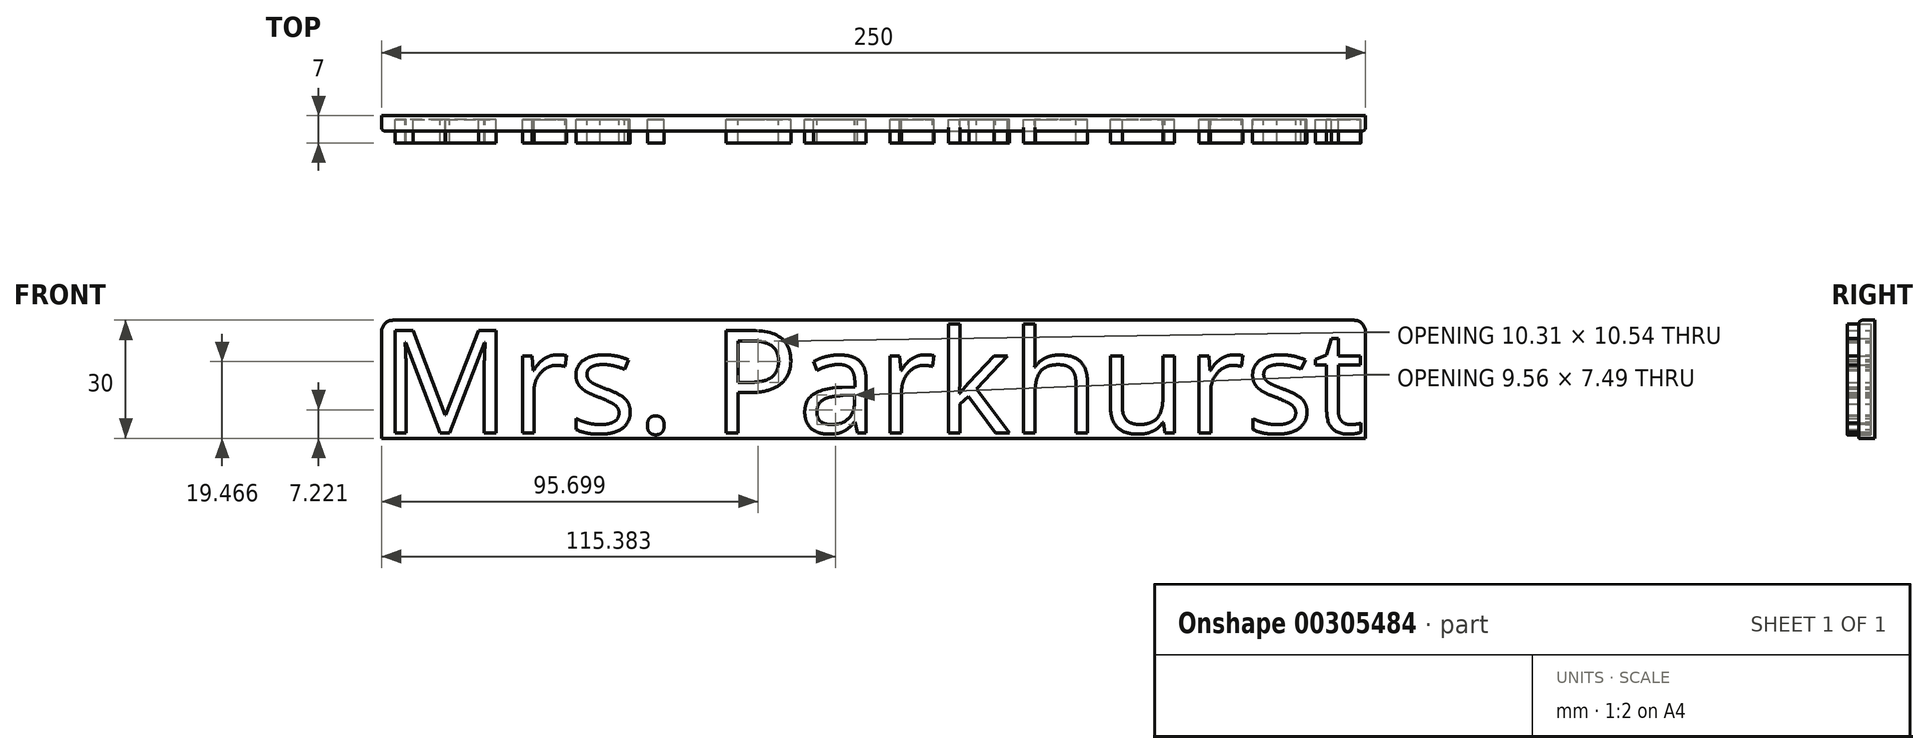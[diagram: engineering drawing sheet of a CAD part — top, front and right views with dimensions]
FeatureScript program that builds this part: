
annotation { "Feature Type Name" : "Feature", "Feature Type Description" : "" }
export const myFeature = defineFeature(function(context is Context, id is Id, definition is map)
    precondition{}
    {
        {
            var Q0;
            Q0=qCreatedBy(makeId("Front.planeOp"),FACE);
            var sketch = newSketch(context, id + "F0", { "sketchPlane" : qUnion([Q0])});
            skText(sketch, "E0", { "text": "Mrs. Parkhurst", "fontName": "OpenSans-Regular.ttf"});
            const initialGuessF0  = {"E0": [-0.12017, 0.0014, 1, 0, 0.02617]};
            skSetInitialGuess(sketch, initialGuessF0);
            skSolve(sketch);
        }
        {
            var Q0;
            Q0=qCreatedBy(makeId("Front.planeOp"),FACE);
            var sketch = newSketch(context, id + "F1", { "sketchPlane" : qUnion([Q0])});
            skLineSegment(sketch, "E1.bottom", {"start": v(-120.02, 30) * mm, "end": v(129.98, 30) * mm});
            skLineSegment(sketch, "E1.top", {"start": v(-120.02, 0) * mm, "end": v(129.98, 0) * mm});
            skLineSegment(sketch, "E1.left", {"start": v(-120.02, 30) * mm, "end": v(-120.02, 0) * mm});
            skLineSegment(sketch, "E1.right", {"start": v(129.98, 30) * mm, "end": v(129.98, 0) * mm});
            skSolve(sketch);
        }
        {
            var Q0;
            Q0 = qSketchRegion(id + "F0", true);
            extrude(context, id + "F2", {"entities" : qUnion([Q0]), "endBound" : BoundingType.SYMMETRIC, "depth" : 6 * mm});
        }
        {
            var Q0;
            Q0 = qSketchRegion(id + "F1", true);
            extrude(context, id + "F3", {"entities" : qUnion([Q0]), "oppositeDirection" : true, "depth" : 4 * mm});
        }
        {
            var Q0;
            Q0=makeQuery(id+"F3.opExtrude","SWEPT_EDGE",EDGE,{"disambiguationData":[OSD([sQuery(id+"F1.wireOp",EDGE,"E1.bottom"),sQuery(id+"F1.wireOp",EDGE,"E1.left")])]});
            var Q1;
            Q1=makeQuery(id+"F3.opExtrude","SWEPT_EDGE",EDGE,{"disambiguationData":[OSD([sQuery(id+"F1.wireOp",EDGE,"E1.bottom"),sQuery(id+"F1.wireOp",EDGE,"E1.right")])]});
            fillet(context, id + "F4", {"entities" : qUnion([Q0, Q1]), "radius" : 3 * mm, "tangentPropagation" : true, "allowEdgeOverflow" : false});
        }
        {
            var Q0;
            Q0=makeQuery(id+"F3.opExtrude","CAP_EDGE",EDGE,{"disambiguationData":[OSD([sQuery(id+"F1.wireOp",EDGE,"E1.left")])],"isStart":true});
            fillet(context, id + "F5", {"entities" : qUnion([Q0]), "radius" : 1 * mm, "tangentPropagation" : true, "allowEdgeOverflow" : false});
        }
    });
